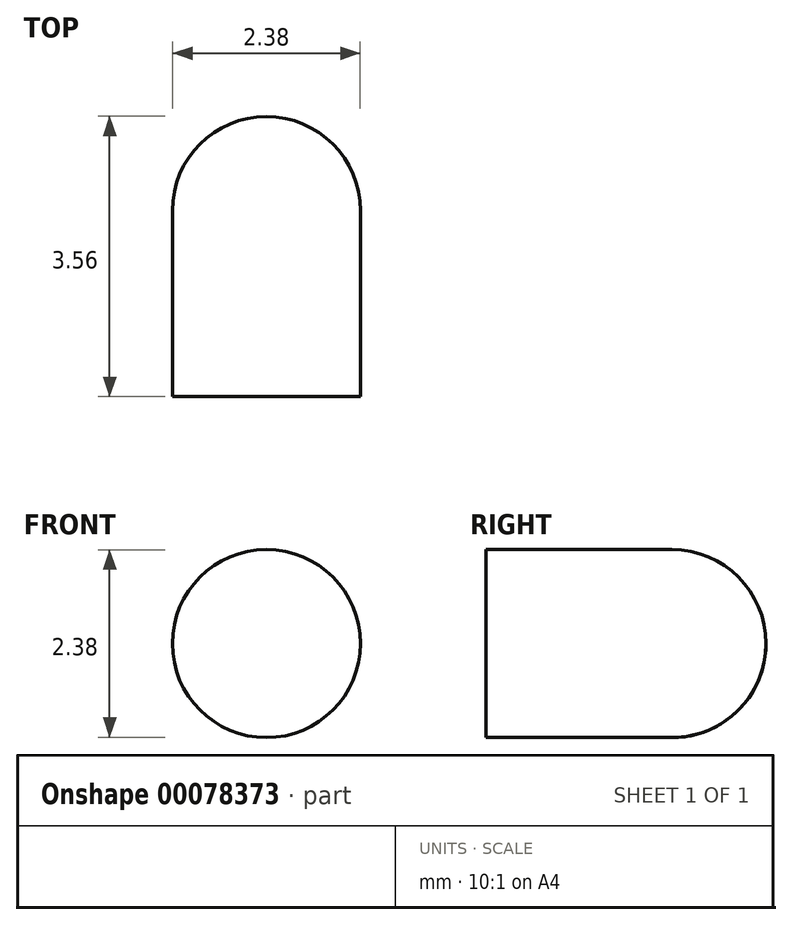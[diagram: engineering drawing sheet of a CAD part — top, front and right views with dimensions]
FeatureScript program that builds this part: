
annotation { "Feature Type Name" : "Feature", "Feature Type Description" : "" }
export const myFeature = defineFeature(function(context is Context, id is Id, definition is map)
    precondition{}
    {
        {
            var Q0;
            Q0=qCreatedBy(makeId("Right.planeOp"),FACE);
            var sketch = newSketch(context, id + "F0", { "sketchPlane" : qUnion([Q0])});
            skLineSegment(sketch, "E0", {"start": v(0, 0) * mm, "end": v(0, 1.2) * mm});
            skLineSegment(sketch, "E1", {"start": v(0, 1.2) * mm, "end": v(2.36, 1.2) * mm});
            skArc(sketch, "E2", {"start": v(3.56, 0) * mm, "mid": v(3.2, 0.84) * mm, "end": v(2.36, 1.2) * mm});
            skLineSegment(sketch, "E3", {"start": v(0, 0) * mm, "end": v(3.56, 0) * mm});
            skSolve(sketch);
        }
        {
            var Q0;
            Q0 = qSketchRegion(id + "F0", true);
            var Q1;
            Q1=sQuery(id+"F0.wireOp",EDGE,"E3");
            revolve(context, id + "F1", {"entities" : qUnion([Q0]), "axis" : qUnion([Q1]), "revolveType" : RevolveType.FULL});
        }
    });
